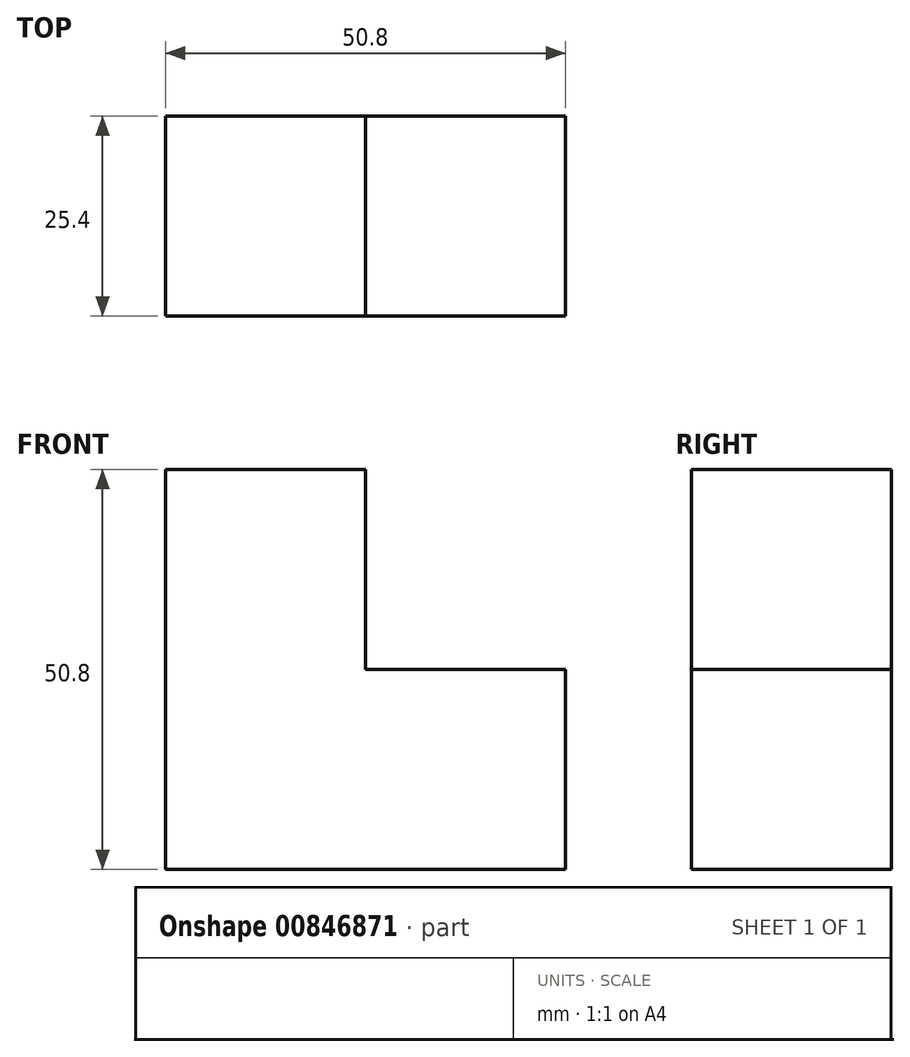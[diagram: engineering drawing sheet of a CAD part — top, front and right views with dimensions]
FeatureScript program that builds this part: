
annotation { "Feature Type Name" : "Feature", "Feature Type Description" : "" }
export const myFeature = defineFeature(function(context is Context, id is Id, definition is map)
    precondition{}
    {
        {
            var Q0;
            Q0=qCreatedBy(makeId("Front.planeOp"),FACE);
            var sketch = newSketch(context, id + "F0", { "sketchPlane" : qUnion([Q0])});
            skLineSegment(sketch, "E0", {"start": v(0, 0) * mm, "end": v(-50.8, 0) * mm});
            skLineSegment(sketch, "E1", {"start": v(-50.8, 0) * mm, "end": v(-50.8, 50.8) * mm});
            skLineSegment(sketch, "E2", {"start": v(-50.8, 50.8) * mm, "end": v(-25.4, 50.8) * mm});
            skLineSegment(sketch, "E3", {"start": v(-25.4, 50.8) * mm, "end": v(-25.4, 25.4) * mm});
            skLineSegment(sketch, "E4", {"start": v(-25.4, 25.4) * mm, "end": v(0, 25.4) * mm});
            skLineSegment(sketch, "E5", {"start": v(0, 0) * mm, "end": v(0, 25.4) * mm});
            skSolve(sketch);
        }
        {
            var Q0;
            Q0=qSketchRegion(id+"F0",true);
            extrude(context, id + "F1", {"entities" : qUnion([Q0]), "depth" : 25.4 * mm, "offsetDistance" : 25.4 * mm});
        }
    });
